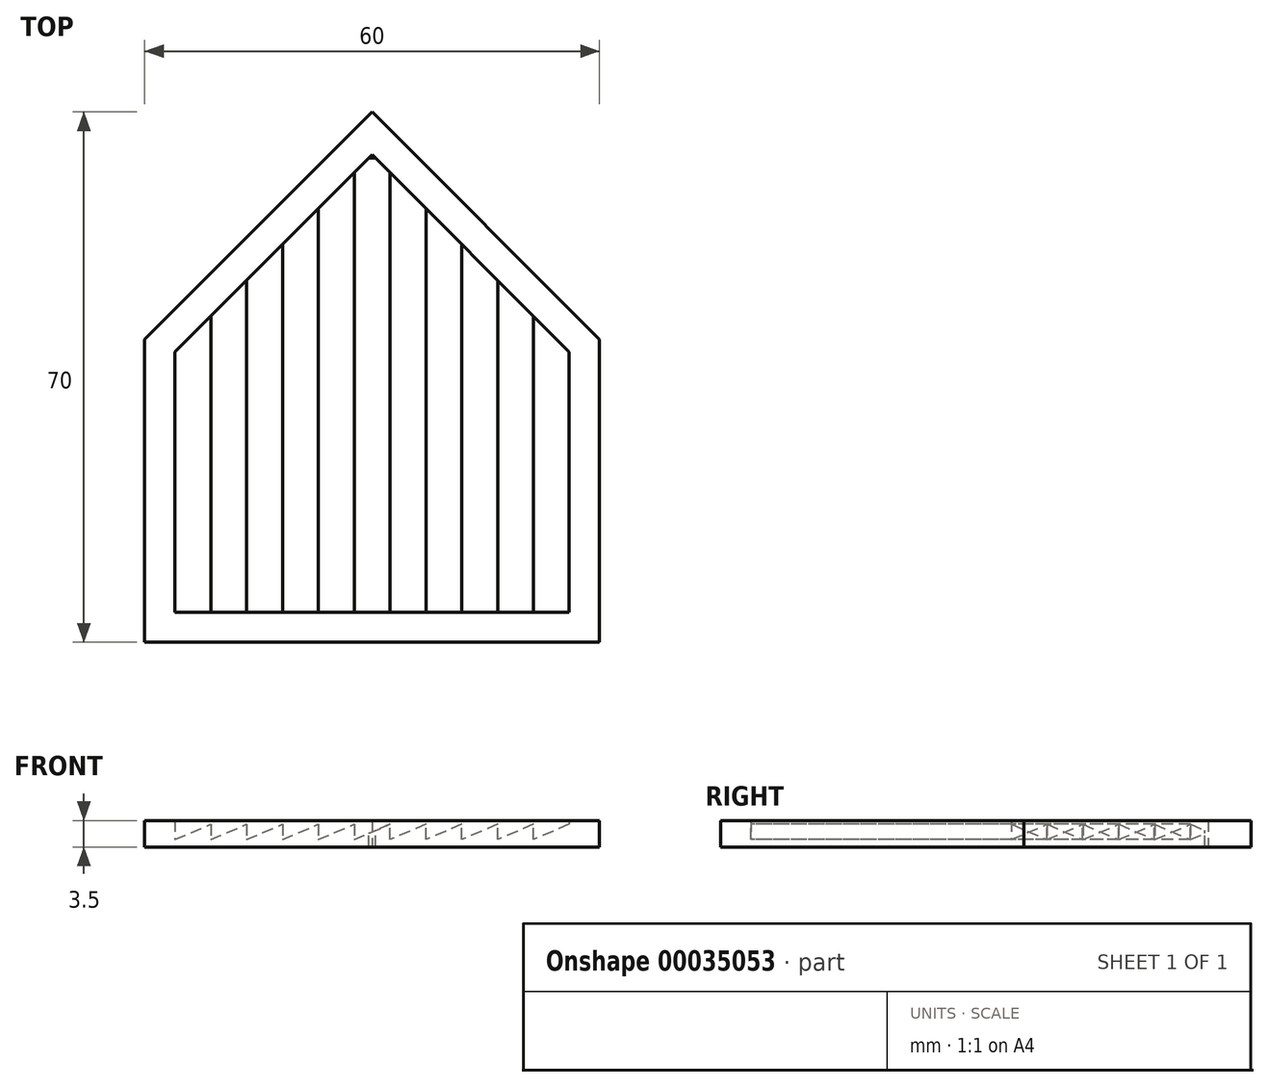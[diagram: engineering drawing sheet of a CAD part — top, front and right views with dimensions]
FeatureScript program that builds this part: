
annotation { "Feature Type Name" : "Feature", "Feature Type Description" : "" }
export const myFeature = defineFeature(function(context is Context, id is Id, definition is map)
    precondition{}
    {
        {
            var Q0;
            Q0=qCreatedBy(makeId("Top.planeOp"),FACE);
            var sketch = newSketch(context, id + "F0", { "sketchPlane" : qUnion([Q0])});
            skLineSegment(sketch, "E0", {"start": v(0, 0) * mm, "end": v(30, 0) * mm});
            skLineSegment(sketch, "E1", {"start": v(30, 0) * mm, "end": v(30, 40) * mm});
            skLineSegment(sketch, "E2", {"start": v(0, 0) * mm, "end": v(-30, 0) * mm});
            skLineSegment(sketch, "E3", {"start": v(-30, 0) * mm, "end": v(-30, 40) * mm});
            skLineSegment(sketch, "E4", {"start": v(0, 0) * mm, "end": v(0, 70) * mm, "construction": true});
            skLineSegment(sketch, "E5", {"start": v(-30, 40) * mm, "end": v(0, 70) * mm});
            skLineSegment(sketch, "E6", {"start": v(0, 70) * mm, "end": v(30, 40) * mm});
            skLineSegment(sketch, "E7.bottom", {"start": v(-30, 0) * mm, "end": v(-26, 0) * mm, "construction": true});
            skLineSegment(sketch, "E7.left", {"start": v(-30, 0) * mm, "end": v(-30, 4) * mm, "construction": true});
            skLineSegment(sketch, "E8.left", {"start": v(30, 40) * mm, "end": v(30, 36) * mm, "construction": true});
            skLineSegment(sketch, "E8.right", {"start": v(26, 38.34) * mm, "end": v(26, 36) * mm, "construction": true});
            skLineSegment(sketch, "E9.bottom", {"start": v(-26, 4) * mm, "end": v(26, 4) * mm});
            skLineSegment(sketch, "E9.left", {"start": v(-26, 4) * mm, "end": v(-26, 38.34) * mm});
            skLineSegment(sketch, "E10", {"start": v(-12.17, 52.17) * mm, "end": v(-26, 38.34) * mm});
            skLineSegment(sketch, "E11", {"start": v(-12.17, 52.17) * mm, "end": v(0, 64.34) * mm});
            skLineSegment(sketch, "E12", {"start": v(0, 64.34) * mm, "end": v(26, 38.34) * mm});
            skLineSegment(sketch, "E13", {"start": v(26, 4) * mm, "end": v(26, 38.34) * mm});
            skSolve(sketch);
        }
        {
            var Q0;
            Q0=qSketchRegion(id+"F0",true);
            extrude(context, id + "F1", {"entities" : qUnion([Q0]), "depth" : 3.5 * mm});
        }
        {
            var Q0;
            Q0=makeQuery(id+"F1.opExtrude","SWEPT_FACE",FACE,{"disambiguationData":[OSD([sQuery(id+"F0.wireOp",EDGE,"E9.bottom")])]});
            var sketch = newSketch(context, id + "F2", { "sketchPlane" : qUnion([Q0])});
            skLineSegment(sketch, "E14", {"start": v(26, 0) * mm, "end": v(26, 1) * mm, "construction": true});
            skLineSegment(sketch, "E15", {"start": v(26, 1) * mm, "end": v(-26, 1) * mm, "construction": true});
            skLineSegment(sketch, "E16", {"start": v(26, 3.5) * mm, "end": v(26, 3) * mm, "construction": true});
            skLineSegment(sketch, "E17", {"start": v(26, 3) * mm, "end": v(-26, 3) * mm, "construction": true});
            skLineSegment(sketch, "E18", {"start": v(26, 1) * mm, "end": v(21.27, 1) * mm, "construction": true});
            skLineSegment(sketch, "E19", {"start": v(21.27, 1) * mm, "end": v(21.27, 3) * mm, "construction": true});
            skLineSegment(sketch, "E20", {"start": v(26, 1) * mm, "end": v(21.27, 3) * mm});
            skLineSegment(sketch, "E21", {"start": v(26, 0) * mm, "end": v(26, 1) * mm});
            skLineSegment(sketch, "E22", {"start": v(21.27, 3) * mm, "end": v(21.27, 1) * mm});
            skLineSegment(sketch, "E23", {"start": v(21.27, 1) * mm, "end": v(16.54, 3) * mm});
            skLineSegment(sketch, "E24", {"start": v(16.54, 3) * mm, "end": v(16.54, 1) * mm});
            skLineSegment(sketch, "E25", {"start": v(16.54, 1) * mm, "end": v(11.8, 3) * mm});
            skLineSegment(sketch, "E26", {"start": v(11.8, 3) * mm, "end": v(11.8, 1) * mm});
            skLineSegment(sketch, "E27", {"start": v(11.8, 1) * mm, "end": v(7.08, 3) * mm});
            skLineSegment(sketch, "E28", {"start": v(7.08, 3) * mm, "end": v(7.08, 1) * mm});
            skLineSegment(sketch, "E29", {"start": v(7.08, 1) * mm, "end": v(2.35, 3) * mm});
            skLineSegment(sketch, "E30", {"start": v(2.35, 3) * mm, "end": v(2.35, 1) * mm});
            skLineSegment(sketch, "E31", {"start": v(2.35, 1) * mm, "end": v(-2.38, 3) * mm});
            skLineSegment(sketch, "E32", {"start": v(-2.38, 3) * mm, "end": v(-2.38, 1) * mm});
            skLineSegment(sketch, "E33", {"start": v(-2.38, 1) * mm, "end": v(-7.11, 3) * mm});
            skLineSegment(sketch, "E34", {"start": v(-7.11, 3) * mm, "end": v(-7.11, 1) * mm});
            skLineSegment(sketch, "E35", {"start": v(-7.11, 1) * mm, "end": v(-11.84, 3) * mm});
            skLineSegment(sketch, "E36", {"start": v(-11.84, 3) * mm, "end": v(-11.84, 1) * mm});
            skLineSegment(sketch, "E37", {"start": v(-11.84, 1) * mm, "end": v(-16.57, 3) * mm});
            skLineSegment(sketch, "E38", {"start": v(-16.57, 3) * mm, "end": v(-16.57, 1) * mm});
            skLineSegment(sketch, "E39", {"start": v(-16.57, 1) * mm, "end": v(-21.3, 3) * mm});
            skLineSegment(sketch, "E40", {"start": v(-21.3, 3) * mm, "end": v(-21.3, 1) * mm});
            skLineSegment(sketch, "E41", {"start": v(-21.3, 1) * mm, "end": v(-26, 3) * mm});
            skLineSegment(sketch, "E42", {"start": v(-26, 3) * mm, "end": v(-26, 0) * mm});
            skLineSegment(sketch, "E43", {"start": v(-26, 0) * mm, "end": v(26, 0) * mm});
            skSolve(sketch);
        }
        {
            var Q0;
            Q0=qSketchRegion(id+"F2",true);
            extrude(context, id + "F3", {"entities" : qUnion([Q0]), "operationType" : NewBodyOperationType.ADD, "depth" : 59.9 * mm});
        }
        {
            var Q0;
            Q0=makeQuery(id+"F1.opExtrude","SWEPT_FACE",FACE,{"disambiguationData":[OSD([sQuery(id+"F0.wireOp",EDGE,"E6")])]});
            var sketch = newSketch(context, id + "F4", { "sketchPlane" : qUnion([Q0])});
            skLineSegment(sketch, "E44.bottom", {"start": v(7.07, 0) * mm, "end": v(49.5, 0) * mm});
            skLineSegment(sketch, "E44.top", {"start": v(7.07, 3.5) * mm, "end": v(49.5, 3.5) * mm});
            skLineSegment(sketch, "E44.left", {"start": v(7.07, 0) * mm, "end": v(7.07, 3.5) * mm});
            skLineSegment(sketch, "E44.right", {"start": v(49.5, 0) * mm, "end": v(49.5, 3.5) * mm});
            skSolve(sketch);
        }
        {
            var Q0;
            Q0=qSketchRegion(id+"F4",true);
            extrude(context, id + "F5", {"entities" : qUnion([Q0]), "operationType" : NewBodyOperationType.REMOVE, "depth" : 25.99 * mm});
        }
        {
            var Q0;
            Q0=makeQuery(id+"F1.opExtrude","SWEPT_FACE",FACE,{"disambiguationData":[OSD([sQuery(id+"F0.wireOp",EDGE,"E5")])]});
            var sketch = newSketch(context, id + "F6", { "sketchPlane" : qUnion([Q0])});
            skLineSegment(sketch, "E45.bottom", {"start": v(-49.5, 3.5) * mm, "end": v(-7.07, 3.5) * mm});
            skLineSegment(sketch, "E45.top", {"start": v(-49.5, 0) * mm, "end": v(-7.07, 0) * mm});
            skLineSegment(sketch, "E45.left", {"start": v(-49.5, 3.5) * mm, "end": v(-49.5, 0) * mm});
            skLineSegment(sketch, "E45.right", {"start": v(-7.07, 3.5) * mm, "end": v(-7.07, 0) * mm});
            skSolve(sketch);
        }
        {
            var Q0;
            Q0=qSketchRegion(id+"F6",true);
            extrude(context, id + "F7", {"entities" : qUnion([Q0]), "operationType" : NewBodyOperationType.REMOVE, "depth" : 37.74 * mm});
        }
    });
